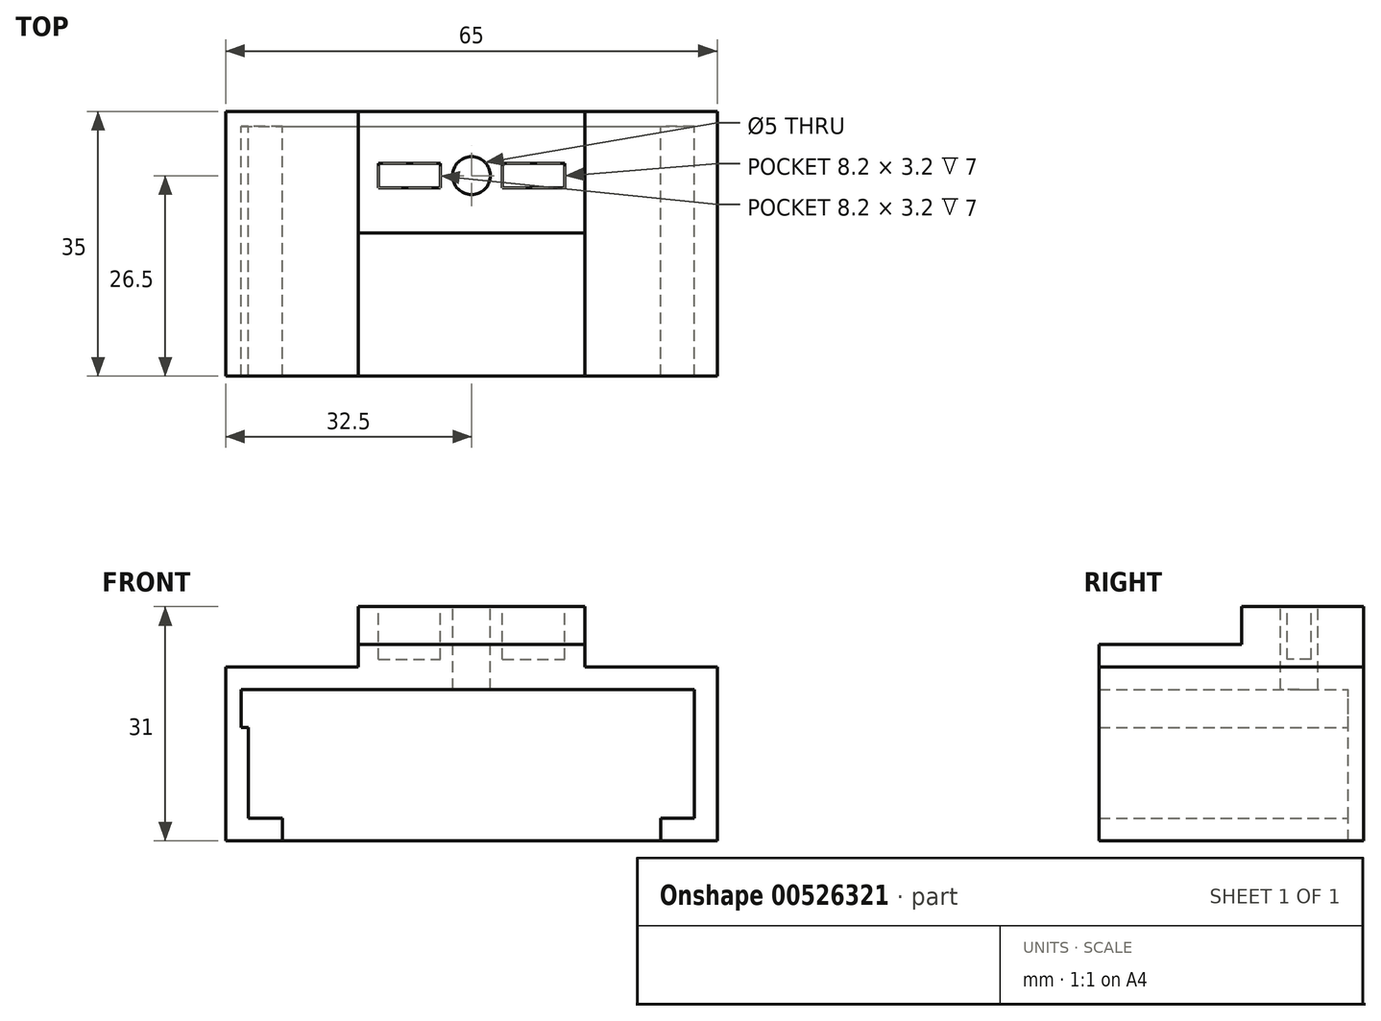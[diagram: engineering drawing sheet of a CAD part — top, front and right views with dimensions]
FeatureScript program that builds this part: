
annotation { "Feature Type Name" : "Feature", "Feature Type Description" : "" }
export const myFeature = defineFeature(function(context is Context, id is Id, definition is map)
    precondition{}
    {
        {
            var Q0;
            Q0=qCreatedBy(makeId("Front.planeOp"),FACE);
            var sketch = newSketch(context, id + "F0", { "sketchPlane" : qUnion([Q0])});
            skLineSegment(sketch, "E0.bottom", {"start": v(-32.5, 11.5) * mm, "end": v(-15, 11.5) * mm});
            skLineSegment(sketch, "E0.top", {"start": v(-32.5, -11.5) * mm, "end": v(-25, -11.5) * mm});
            skLineSegment(sketch, "E0.left", {"start": v(-32.5, 11.5) * mm, "end": v(-32.5, -11.5) * mm});
            skLineSegment(sketch, "E0.right", {"start": v(32.5, 11.5) * mm, "end": v(32.5, -11.5) * mm});
            skPoint(sketch, "E0.middle", {"position": v(0, 0) * mm});
            skLineSegment(sketch, "E1", {"start": v(0, 0) * mm, "end": v(0, 8.5) * mm, "construction": true});
            skLineSegment(sketch, "E2", {"start": v(-15, 11.5) * mm, "end": v(-15, 19.5) * mm});
            skLineSegment(sketch, "E3", {"start": v(-15, 19.5) * mm, "end": v(0, 19.5) * mm});
            skLineSegment(sketch, "E4.bottom", {"start": v(-29.5, 8.5) * mm, "end": v(29.5, 8.5) * mm});
            skLineSegment(sketch, "E4.top", {"start": v(-29.5, -8.5) * mm, "end": v(-25, -8.5) * mm});
            skLineSegment(sketch, "E4.left", {"start": v(-29.5, 3.5) * mm, "end": v(-29.5, -8.5) * mm});
            skLineSegment(sketch, "E4.right", {"start": v(29.5, 8.5) * mm, "end": v(29.5, -8.5) * mm});
            skLineSegment(sketch, "E5", {"start": v(-29.5, 8.5) * mm, "end": v(-30.5, 8.5) * mm});
            skLineSegment(sketch, "E6", {"start": v(-30.5, 8.5) * mm, "end": v(-30.5, 3.5) * mm});
            skLineSegment(sketch, "E7", {"start": v(-30.5, 3.5) * mm, "end": v(-29.5, 3.5) * mm});
            skLineSegment(sketch, "E8", {"start": v(-25, -8.5) * mm, "end": v(-25, -11.5) * mm});
            skLineSegment(sketch, "E9.MirrorCS", {"start": v(25, -8.5) * mm, "end": v(25, -11.5) * mm});
            skLineSegment(sketch, "E10.trimOffspring", {"start": v(25, -8.5) * mm, "end": v(29.5, -8.5) * mm});
            skLineSegment(sketch, "E11.trimOffspring", {"start": v(25, -11.5) * mm, "end": v(32.5, -11.5) * mm});
            skLineSegment(sketch, "E12.trimOffspring", {"start": v(15, 11.5) * mm, "end": v(32.5, 11.5) * mm});
            skLineSegment(sketch, "E13.MirrorCS", {"start": v(15, 11.5) * mm, "end": v(15, 19.5) * mm});
            skLineSegment(sketch, "E14.MirrorCS", {"start": v(15, 19.5) * mm, "end": v(0, 19.5) * mm});
            skLineSegment(sketch, "E15.trimOffspring", {"start": v(0, 19.5) * mm, "end": v(0, 38.4) * mm, "construction": true});
            skSolve(sketch);
        }
        {
            var Q0;
            Q0 = qSketchRegion(id + "F0", true);
            extrude(context, id + "F1", {"entities" : qUnion([Q0]), "depth" : 35 * mm, "offsetDistance" : 25 * mm});
        }
        {
            var Q0;
            Q0=makeQuery(id+"F1.opExtrude","CAP_FACE",FACE,{"disambiguationData":[OSD([sQuery(id+"F0.wireOp",EDGE,"E0.bottom"),sQuery(id+"F0.wireOp",EDGE,"E0.top"),sQuery(id+"F0.wireOp",EDGE,"E0.left"),sQuery(id+"F0.wireOp",EDGE,"E0.right"),sQuery(id+"F0.wireOp",EDGE,"E2"),sQuery(id+"F0.wireOp",EDGE,"E3"),sQuery(id+"F0.wireOp",EDGE,"E4.bottom"),sQuery(id+"F0.wireOp",EDGE,"E4.top"),sQuery(id+"F0.wireOp",EDGE,"E4.left"),sQuery(id+"F0.wireOp",EDGE,"E4.right"),sQuery(id+"F0.wireOp",EDGE,"E5"),sQuery(id+"F0.wireOp",EDGE,"E6"),sQuery(id+"F0.wireOp",EDGE,"E7"),sQuery(id+"F0.wireOp",EDGE,"E8"),sQuery(id+"F0.wireOp",EDGE,"E9.MirrorCS"),sQuery(id+"F0.wireOp",EDGE,"E10.trimOffspring"),sQuery(id+"F0.wireOp",EDGE,"E11.trimOffspring"),sQuery(id+"F0.wireOp",EDGE,"E12.trimOffspring"),sQuery(id+"F0.wireOp",EDGE,"E13.MirrorCS"),sQuery(id+"F0.wireOp",EDGE,"E14.MirrorCS")])],"isStart":true});
            var sketch = newSketch(context, id + "F2", { "sketchPlane" : qUnion([Q0])});
            skLineSegment(sketch, "E16.1", {"start": v(-32.5, 11.5) * mm, "end": v(-32.5, -11.5) * mm});
            skLineSegment(sketch, "E16.5", {"start": v(-25, -11.5) * mm, "end": v(-32.5, -11.5) * mm});
            skLineSegment(sketch, "E16.8", {"start": v(32.5, -11.5) * mm, "end": v(25, -11.5) * mm});
            skLineSegment(sketch, "E16.9", {"start": v(32.5, 11.5) * mm, "end": v(32.5, -11.5) * mm});
            skLineSegment(sketch, "E16.13", {"start": v(-15, 11.5) * mm, "end": v(-32.5, 11.5) * mm});
            skLineSegment(sketch, "E16.14", {"start": v(-15, 11.5) * mm, "end": v(-15, 19.5) * mm});
            skLineSegment(sketch, "E16.15", {"start": v(-15, 19.5) * mm, "end": v(15, 19.5) * mm});
            skLineSegment(sketch, "E16.16", {"start": v(15, 11.5) * mm, "end": v(15, 19.5) * mm});
            skLineSegment(sketch, "E16.17", {"start": v(32.5, 11.5) * mm, "end": v(15, 11.5) * mm});
            skPoint(sketch, "E16.18", {"position": v(-23.75, 11.5) * mm});
            skLineSegment(sketch, "E17", {"start": v(-25, -11.5) * mm, "end": v(25, -11.5) * mm});
            skSolve(sketch);
        }
        {
            var Q0;
            Q0 = qSketchRegion(id + "F2", true);
            extrude(context, id + "F3", {"entities" : qUnion([Q0]), "operationType" : NewBodyOperationType.ADD, "oppositeDirection" : true, "depth" : 2 * mm, "offsetDistance" : 25 * mm});
        }
        {
            var Q0;
            Q0=makeQuery(id+"F1.opExtrude","SWEPT_FACE",FACE,{"disambiguationData":[OSD([sQuery(id+"F0.wireOp",EDGE,"E3"),sQuery(id+"F0.wireOp",EDGE,"E14.MirrorCS")])]});
            var sketch = newSketch(context, id + "F4", { "sketchPlane" : qUnion([Q0])});
            skCircle(sketch, "E18", {"center": v(0, -8.5) * mm, "radius": 2.5 * mm});
            skSolve(sketch);
        }
        {
            var Q0;
            Q0 = qSketchRegion(id + "F4", true);
            extrude(context, id + "F5", {"entities" : qUnion([Q0]), "operationType" : NewBodyOperationType.REMOVE, "oppositeDirection" : true, "depth" : 25 * mm, "offsetDistance" : 25 * mm});
        }
        {
            var Q0;
            Q0=makeQuery(id+"F1.opExtrude","SWEPT_FACE",FACE,{"disambiguationData":[OSD([sQuery(id+"F0.wireOp",EDGE,"E3"),sQuery(id+"F0.wireOp",EDGE,"E14.MirrorCS")])]});
            var sketch = newSketch(context, id + "F6", { "sketchPlane" : qUnion([Q0])});
            skLineSegment(sketch, "E19.bottom", {"start": v(-12.3, -6.9) * mm, "end": v(-4.1, -6.9) * mm});
            skLineSegment(sketch, "E19.top", {"start": v(-12.3, -10.1) * mm, "end": v(-4.1, -10.1) * mm});
            skLineSegment(sketch, "E19.left", {"start": v(-12.3, -6.9) * mm, "end": v(-12.3, -10.1) * mm});
            skLineSegment(sketch, "E19.right", {"start": v(12.3, -6.9) * mm, "end": v(12.3, -10.1) * mm});
            skPoint(sketch, "E19.middle", {"position": v(0, -8.5) * mm});
            skLineSegment(sketch, "E20", {"start": v(-4.1, -6.9) * mm, "end": v(-4.1, -10.1) * mm});
            skLineSegment(sketch, "E21", {"start": v(0, -8.5) * mm, "end": v(0, 2.8) * mm, "construction": true});
            skLineSegment(sketch, "E22.MirrorCS", {"start": v(4.1, -6.9) * mm, "end": v(4.1, -10.1) * mm});
            skLineSegment(sketch, "E23.trimOffspring", {"start": v(4.1, -6.9) * mm, "end": v(12.3, -6.9) * mm});
            skLineSegment(sketch, "E24.trimOffspring", {"start": v(4.1, -10.1) * mm, "end": v(12.3, -10.1) * mm});
            skSolve(sketch);
        }
        {
            var Q0;
            Q0 = qSketchRegion(id + "F6", true);
            extrude(context, id + "F7", {"entities" : qUnion([Q0]), "operationType" : NewBodyOperationType.REMOVE, "oppositeDirection" : true, "depth" : 7 * mm, "offsetDistance" : 25 * mm});
        }
        {
            var Q0;
            Q0=makeQuery(id+"F1.opExtrude","SWEPT_FACE",FACE,{"disambiguationData":[OSD([sQuery(id+"F0.wireOp",EDGE,"E3"),sQuery(id+"F0.wireOp",EDGE,"E14.MirrorCS")])]});
            var sketch = newSketch(context, id + "F8", { "sketchPlane" : qUnion([Q0])});
            skLineSegment(sketch, "E25.bottom", {"start": v(-15, -35) * mm, "end": v(15, -35) * mm});
            skLineSegment(sketch, "E25.top", {"start": v(-15, -16.1) * mm, "end": v(15, -16.1) * mm});
            skLineSegment(sketch, "E25.left", {"start": v(-15, -35) * mm, "end": v(-15, -16.1) * mm});
            skLineSegment(sketch, "E25.right", {"start": v(15, -35) * mm, "end": v(15, -16.1) * mm});
            skSolve(sketch);
        }
        {
            var Q0;
            Q0 = qSketchRegion(id + "F8", true);
            extrude(context, id + "F9", {"entities" : qUnion([Q0]), "operationType" : NewBodyOperationType.REMOVE, "oppositeDirection" : true, "depth" : 5 * mm, "offsetDistance" : 25 * mm});
        }
    });
